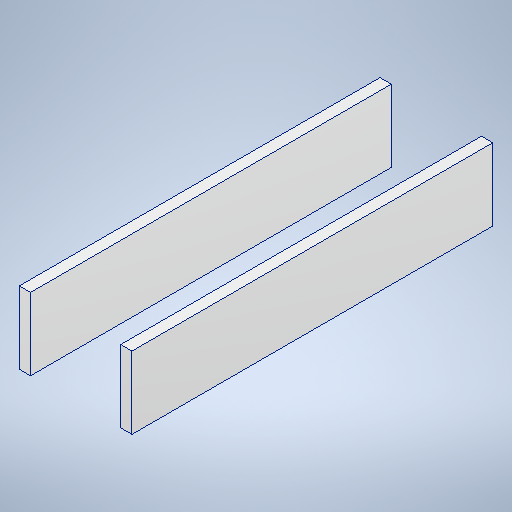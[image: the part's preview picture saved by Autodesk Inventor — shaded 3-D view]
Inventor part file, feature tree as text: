
AUTODESK INVENTOR PART (.ipt)
format: ipt  version: 2025.1 (Build 291241000, 241)  size: 216,576 bytes
history: native  units: mm
features: extrude x1, sketch x1
ambient origin geometry x8: Origin, YZ Plane, XZ Plane, XY Plane, X Axis, Y Axis, Z Axis, Center Point
bodies: Solid1 (feature_tree)
feature tree (2):
  extrude  "Extrusion1"  Depth=5.0mm
  sketch  "Sketch1"  dims[d0=50.0mm d1=5.0mm d2=32.0mm d3=16.0mm d5=0.0mm]
